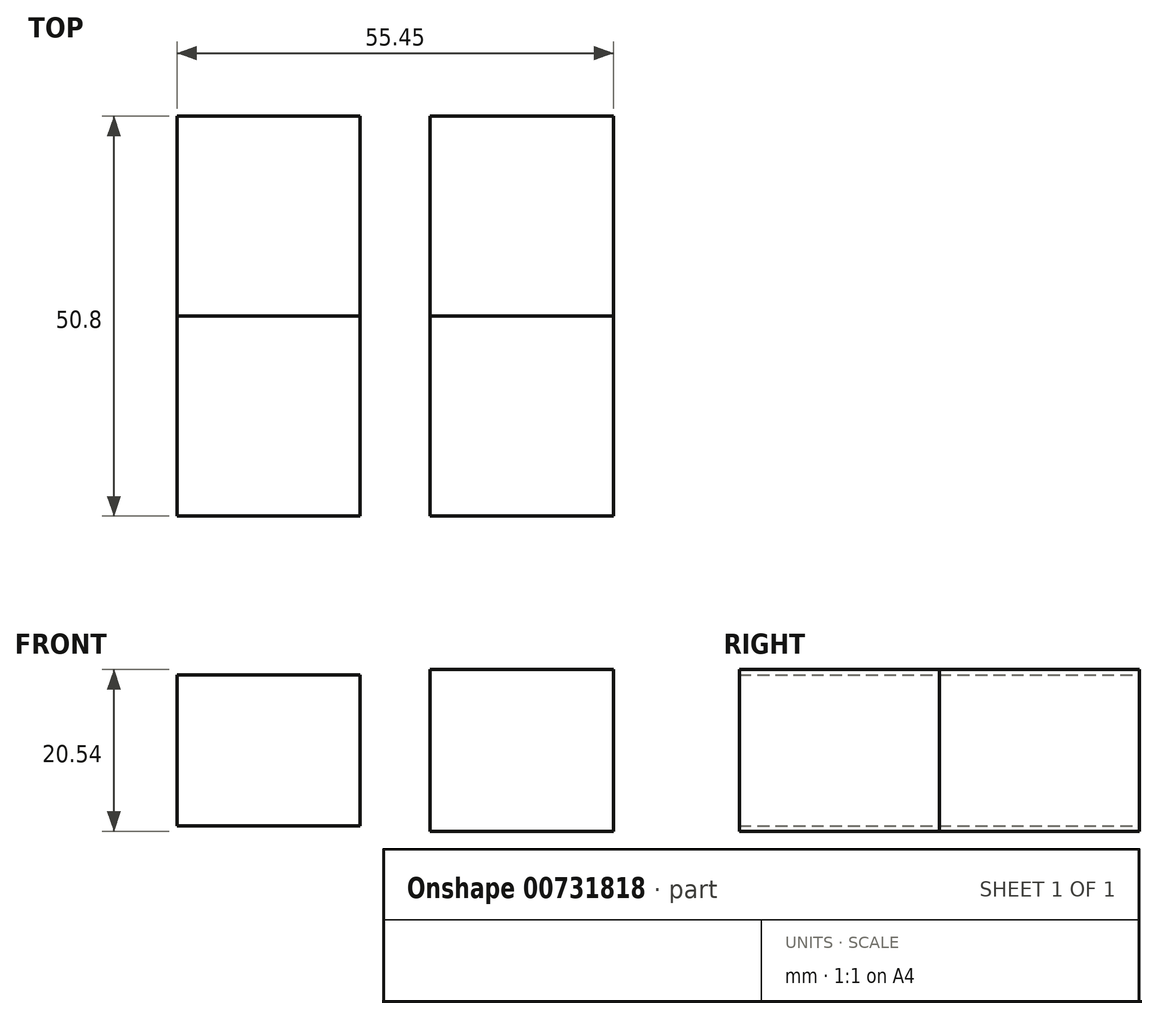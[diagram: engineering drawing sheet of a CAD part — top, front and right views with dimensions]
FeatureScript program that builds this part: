
annotation { "Feature Type Name" : "Feature", "Feature Type Description" : "" }
export const myFeature = defineFeature(function(context is Context, id is Id, definition is map)
    precondition{}
    {
        {
            var Q0;
            Q0=qCreatedBy(makeId("Front.planeOp"),FACE);
            var sketch = newSketch(context, id + "F0", { "sketchPlane" : qUnion([Q0])});
            skLineSegment(sketch, "E0", {"start": v(0, 0) * mm, "end": v(-177.8, 0) * mm});
            skSolve(sketch);
        }
        {
            var Q0;
            Q0=qCreatedBy(makeId("Front.planeOp"),FACE);
            var sketch = newSketch(context, id + "F1", { "sketchPlane" : qUnion([Q0])});
            skLineSegment(sketch, "E1", {"start": v(0, 0) * mm, "end": v(11.53, -5.33) * mm});
            skLineSegment(sketch, "E2", {"start": v(11.53, -5.33) * mm, "end": v(49.63, -5.33) * mm});
            skLineSegment(sketch, "E3", {"start": v(49.63, -5.33) * mm, "end": v(49.63, 7.37) * mm});
            skLineSegment(sketch, "E4", {"start": v(49.63, 7.37) * mm, "end": v(11.53, 7.37) * mm});
            skLineSegment(sketch, "E5", {"start": v(11.53, 7.37) * mm, "end": v(11.53, 32.77) * mm});
            skLineSegment(sketch, "E6", {"start": v(11.53, 32.77) * mm, "end": v(49.63, 32.77) * mm});
            skLineSegment(sketch, "E7", {"start": v(49.63, 32.77) * mm, "end": v(49.63, 58.17) * mm});
            skLineSegment(sketch, "E8", {"start": v(49.63, 58.17) * mm, "end": v(-13.87, 58.17) * mm});
            skLineSegment(sketch, "E9", {"start": v(-13.87, 58.17) * mm, "end": v(-45.04, 36.25) * mm});
            skLineSegment(sketch, "E10", {"start": v(-45.04, 36.25) * mm, "end": v(-108.54, 36.25) * mm});
            skLineSegment(sketch, "E11", {"start": v(-108.54, 36.25) * mm, "end": v(-131, 48.13) * mm});
            skSolve(sketch);
        }
        {
            var Q0;
            Q0=qCreatedBy(makeId("Front.planeOp"),FACE);
            var sketch = newSketch(context, id + "F2", { "sketchPlane" : qUnion([Q0])});
            skLineSegment(sketch, "E12", {"start": v(-131, 48.13) * mm, "end": v(-178.2, 48.13) * mm});
            skSolve(sketch);
        }
        {
            var Q0;
            Q0=qCreatedBy(makeId("Front.planeOp"),FACE);
            var sketch = newSketch(context, id + "F3", { "sketchPlane" : qUnion([Q0])});
            skLineSegment(sketch, "E13", {"start": v(-178.38, 48.68) * mm, "end": v(-178.38, 35.98) * mm});
            skLineSegment(sketch, "E14", {"start": v(-178.38, 35.98) * mm, "end": v(-140.28, 35.98) * mm});
            skLineSegment(sketch, "E15", {"start": v(-140.28, 35.98) * mm, "end": v(-129.6, 29.11) * mm});
            skLineSegment(sketch, "E16", {"start": v(-129.6, 29.11) * mm, "end": v(-178.38, 29.11) * mm});
            skLineSegment(sketch, "E17", {"start": v(-178.38, 29.11) * mm, "end": v(-178.38, 16.41) * mm});
            skLineSegment(sketch, "E18", {"start": v(-178.38, 16.41) * mm, "end": v(-127.58, 16.41) * mm});
            skLineSegment(sketch, "E19", {"start": v(-127.58, 16.41) * mm, "end": v(-127.58, 3.71) * mm});
            skLineSegment(sketch, "E20", {"start": v(-127.58, 3.71) * mm, "end": v(-178.38, 3.71) * mm});
            skLineSegment(sketch, "E21", {"start": v(-178.38, 3.71) * mm, "end": v(-178.38, 0) * mm});
            skSolve(sketch);
        }
        {
            var Q0;
            Q0=qCreatedBy(makeId("Front.planeOp"),FACE);
            var sketch = newSketch(context, id + "F4", { "sketchPlane" : qUnion([Q0])});
            skLineSegment(sketch, "E22.bottom", {"start": v(-91.4, 8.79) * mm, "end": v(-114.67, 8.79) * mm});
            skLineSegment(sketch, "E22.top", {"start": v(-91.4, 27.95) * mm, "end": v(-114.67, 27.95) * mm});
            skLineSegment(sketch, "E22.left", {"start": v(-91.4, 8.79) * mm, "end": v(-91.4, 27.95) * mm});
            skLineSegment(sketch, "E22.right", {"start": v(-114.67, 8.79) * mm, "end": v(-114.67, 27.95) * mm});
            skPoint(sketch, "E22.middle", {"position": v(-103.03, 18.37) * mm});
            skSolve(sketch);
        }
        {
            var Q0;
            Q0=qCreatedBy(makeId("Front.planeOp"),FACE);
            var sketch = newSketch(context, id + "F5", { "sketchPlane" : qUnion([Q0])});
            skLineSegment(sketch, "E23.bottom", {"start": v(-59.22, 8.1) * mm, "end": v(-82.5, 8.1) * mm});
            skLineSegment(sketch, "E23.top", {"start": v(-59.22, 28.64) * mm, "end": v(-82.5, 28.64) * mm});
            skLineSegment(sketch, "E23.left", {"start": v(-59.22, 8.1) * mm, "end": v(-59.22, 28.64) * mm});
            skLineSegment(sketch, "E23.right", {"start": v(-82.5, 8.1) * mm, "end": v(-82.5, 28.64) * mm});
            skPoint(sketch, "E23.middle", {"position": v(-70.86, 18.37) * mm});
            skSolve(sketch);
        }
        {
            var Q0;
            Q0=qCreatedBy(makeId("Front.planeOp"),FACE);
            var sketch = newSketch(context, id + "F6", { "sketchPlane" : qUnion([Q0])});
            skLineSegment(sketch, "E24", {"start": v(-45.2, 8.07) * mm, "end": v(-45.2, 24.53) * mm});
            skLineSegment(sketch, "E25", {"start": v(-45.2, 24.53) * mm, "end": v(-32.14, 33.73) * mm});
            skSolve(sketch);
        }
        {
            var Q0;
            Q0=makeQuery(id+"F5.imprint","IMPRINT",FACE,{"disambiguationData":[TD([[makeQuery(id+"F5.imprint","IMPRINT",EDGE,{"derivedFrom":sQuery(id+"F5.wireOp",EDGE,"E23.bottom")}),-1.0]])]});
            var Q1;
            Q1=makeQuery(id+"F4.imprint","IMPRINT",FACE,{"disambiguationData":[TD([[makeQuery(id+"F4.imprint","IMPRINT",EDGE,{"derivedFrom":sQuery(id+"F4.wireOp",EDGE,"E22.bottom")}),-1.0]])]});
            extrude(context, id + "F7", {"entities" : qUnion([Q0, Q1]), "depth" : 25.4 * mm, "offsetDistance" : 25.4 * mm});
        }
        {
            var Q0;
            Q0 = qSketchRegion(id + "F0", true);
            var Q1;
            Q1 = qSketchRegion(id + "F1", true);
            var Q2;
            Q2 = qSketchRegion(id + "F2", true);
            var Q3;
            Q3 = qSketchRegion(id + "F3", true);
            var Q4;
            Q4 = qSketchRegion(id + "F4", true);
            var Q5;
            Q5 = qSketchRegion(id + "F5", true);
            var Q6;
            Q6 = qSketchRegion(id + "F6", true);
            extrude(context, id + "F8", {"entities" : qUnion([Q0, Q1, Q2, Q3, Q4, Q5, Q6]), "depth" : 25.4 * mm, "offsetDistance" : 25.4 * mm});
        }
        {
            var Q0;
            Q0=makeQuery(id+"F7.opExtrude","CAP_FACE",FACE,{"disambiguationData":[OSD([sQuery(id+"F4.wireOp",EDGE,"E22.bottom"),sQuery(id+"F4.wireOp",EDGE,"E22.top"),sQuery(id+"F4.wireOp",EDGE,"E22.left"),sQuery(id+"F4.wireOp",EDGE,"E22.right")])],"isStart":false});
            var Q1;
            Q1=makeQuery(id+"F7.opExtrude","CAP_FACE",FACE,{"disambiguationData":[OSD([sQuery(id+"F5.wireOp",EDGE,"E23.bottom"),sQuery(id+"F5.wireOp",EDGE,"E23.top"),sQuery(id+"F5.wireOp",EDGE,"E23.left"),sQuery(id+"F5.wireOp",EDGE,"E23.right")])],"isStart":false});
            extrude(context, id + "F9", {"entities" : qUnion([Q0, Q1]), "depth" : 25.4 * mm, "offsetDistance" : 25.4 * mm});
        }
    });
